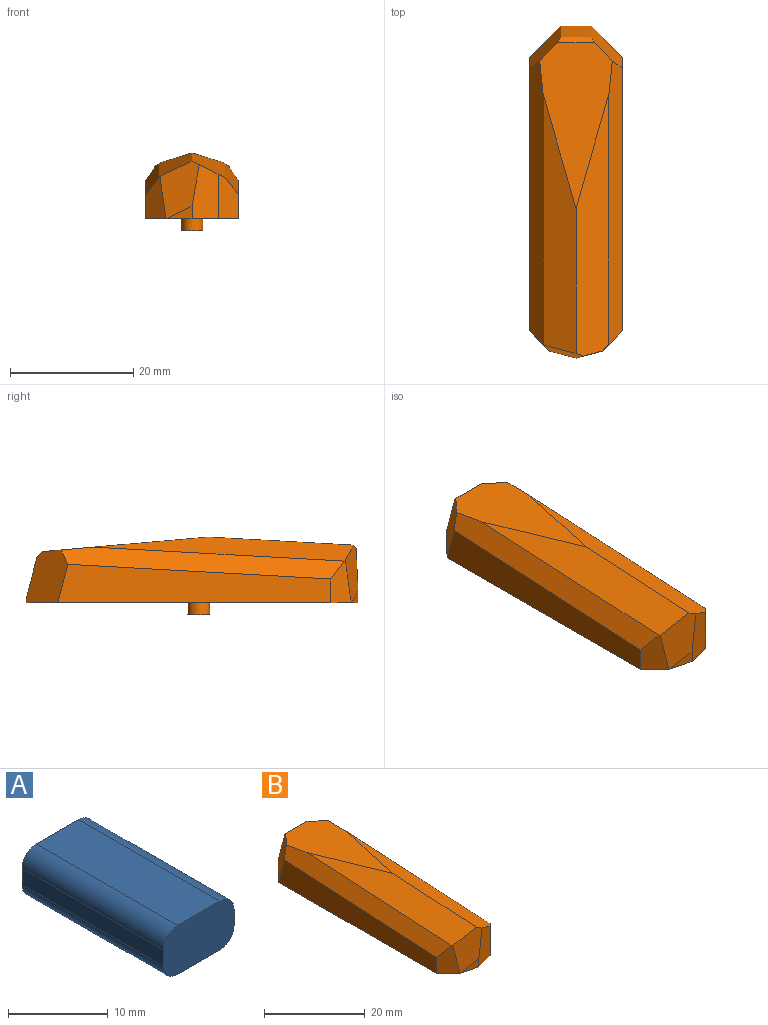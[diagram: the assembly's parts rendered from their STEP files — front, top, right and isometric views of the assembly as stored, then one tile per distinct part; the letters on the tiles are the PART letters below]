
ASSEMBLY  parts=2 mates=1
PART A: 10 faces, bbox 10x20x6 mm
  f0: plane 20x6mm, normal (0,0,-1), area 120mm2, adj f1,f2,f4,f8
  f1: cylinder r=2mm len=20mm, axis (0,1,0), area 62.8mm2, adj f0,f2,f4,f9
  f2: plane 10x6mm, normal (0,1,0), area 56.6mm2, adj f0,f1,f3,f5,f6,f7,f8,f9
  f3: cylinder r=2mm len=20mm, axis (0,-1,0), area 62.8mm2, adj f2,f4,f5,f9
  f4: plane 10x6mm, normal (0,-1,0), area 56.6mm2, adj f0,f1,f3,f5,f6,f7,f8,f9
  f5: plane 20x6mm, normal (0,0,1), area 120mm2, adj f2,f3,f4,f6
  f6: cylinder r=2mm len=20mm, axis (0,1,0), area 62.8mm2, adj f2,f4,f5,f7
  f7: plane 20x2mm, normal (1,0,0), area 40mm2, adj f2,f4,f6,f8
  f8: cylinder r=2mm len=20mm, axis (0,-1,0), area 62.8mm2, adj f0,f2,f4,f7
  f9: plane 20x2mm, normal (-1,0,0), area 40mm2, adj f1,f2,f3,f4
PART B: 51 faces, bbox 15x53.8x12.6 mm
  f0: plane 44.26x6.22mm, normal (1,0,0), area 219.2mm2, adj f1,f9,f10,f49
  f1: plane 45.86x5.16mm, normal (0.81,-0.03,0.58), area 162.1mm2, adj f0,f2,f8,f9,f49
  f2: plane 26.95x11.76mm, normal (0,0.09,1), area 186.4mm2, adj f1,f3,f5,f6,f7,f8,f49
  f3: plane 5.95x0.85mm, normal (0,0.71,0.71), area 6.4mm2, adj f2,f4,f5,f49
  f4: plane 6.88x4.74mm, normal (0,0.97,0.25), area 33.7mm2, adj f3,f5,f49,f50
  f5: plane 8.53x6.79mm, normal (-0.71,0.68,0.18), area 60mm2, adj f2,f3,f4,f6,f10,f44,f50
  f6: plane 45.86x5.16mm, normal (-0.81,-0.03,0.58), area 162.1mm2, adj f2,f5,f7,f44,f45
  f7: plane 42.1x5.34mm, normal (-0.45,-0.05,0.89), area 191.9mm2, adj f2,f6,f8,f45,f46
  f8: plane 42.53x5.34mm, normal (0.45,-0.05,0.89), area 195.2mm2, adj f1,f2,f7,f9,f46,f47
  f9: plane 7.22x3.28mm, normal (0.71,-0.71,0), area 27.2mm2, adj f0,f1,f8,f10,f47
  f10: plane 53.81x15mm, normal (0,0,-1), area 208.9mm2, adj f0,f5,f9,f11,f13,f15,f16,f32
  f11: plane 3.57x2.3mm, normal (0,-1,0), area 8.2mm2, adj f10,f12,f13,f36
  f12: plane 4.5x3.85mm, normal (0,-0.97,-0.25), area 17.8mm2, adj f11,f13,f14,f35,f36,f37
  f13: plane 4.15x4.01mm, normal (0.72,-0.7,0), area 16.4mm2, adj f10,f11,f12,f14,f15
  f14: plane 4.97x4.55mm, normal (0.71,-0.68,-0.18), area 24.6mm2, adj f12,f13,f15,f17,f24,f37
  f15: plane 42.87x6.53mm, normal (1,0,0), area 228.9mm2, adj f10,f13,f14,f16,f17
  f16: plane 6.31x2.24mm, normal (0.71,0.71,0), area 17.4mm2, adj f10,f15,f17,f30,f32
  f17: plane 43.56x3.75mm, normal (0.81,0.03,-0.58), area 87.8mm2, adj f14,f15,f16,f18,f19,f20,f24,f30
  f18: plane 9.43x1.2mm, normal (0,0,-1), area 11.3mm2, adj f17,f20,f38,f41
  f19: plane 10.17x1.2mm, normal (0,0,-1), area 12.1mm2, adj f17,f38,f39,f40
  f20: plane 9.34x1.64mm, normal (0,-1,0), area 10.7mm2, adj f17,f18,f22,f27,f30,f38
  f21: plane 1.29x0.68mm, normal (0,-0.09,-1), area 0.4mm2, adj f25,f26,f29
  f22: plane 3.38x3.24mm, normal (0,-0.09,-1), area 7.6mm2, adj f20,f27,f30,f42
  f23: plane 8.51x8mm, normal (0,-0.09,-1), area 49.9mm2, adj f28,f31,f40,f41
  f24: plane 10.39x9.42mm, normal (0,-0.09,-1), area 84.4mm2, adj f14,f17,f35,f37,f38,f39
  f25: cylinder r=0.65mm len=11.33mm, axis (0,0,-1), area 45.5mm2, adj f21,f26,f29,f43
  f26: plane 1.2x0.66mm, normal (-0.45,0.05,-0.89), area 0.5mm2, adj f21,f25,f29
  f27: plane 27.96x4.54mm, normal (-0.45,0.05,-0.89), area 132mm2, adj f20,f22,f30,f32,f33,f38,f42
  f28: plane 8x2.58mm, normal (-0.45,0.05,-0.89), area 12.8mm2, adj f23,f38,f40,f41
  f29: plane 1.2x0.66mm, normal (0.45,0.05,-0.89), area 0.5mm2, adj f21,f25,f26
  f30: plane 27.96x4.54mm, normal (0.45,0.05,-0.89), area 132mm2, adj f16,f17,f20,f22,f27,f32,f42
  f31: plane 8x2.58mm, normal (0.45,0.05,-0.89), area 12.8mm2, adj f17,f23,f40,f41
  f32: plane 8.09x7.12mm, normal (0,1,0), area 51.2mm2, adj f10,f16,f27,f30,f33
  f33: plane 6.31x2.24mm, normal (-0.71,0.71,0), area 17.4mm2, adj f10,f27,f32,f34,f38
  f34: plane 42.87x6.53mm, normal (-1,0,0), area 228.9mm2, adj f10,f33,f35,f36,f38
  f35: plane 4.97x4.55mm, normal (-0.71,-0.68,-0.18), area 24.6mm2, adj f12,f24,f34,f36,f37,f38
  f36: plane 4.15x4.01mm, normal (-0.72,-0.7,0), area 16.4mm2, adj f10,f11,f12,f34,f35
  f37: plane 4.29x0.31mm, normal (0,-0.71,-0.71), area 1.8mm2, adj f12,f14,f24,f35
  f38: plane 43.56x3.75mm, normal (-0.81,0.03,-0.58), area 87.8mm2, adj f18,f19,f20,f24,f27,f28,f33,f34
  f39: plane 10.17x0.73mm, normal (0,1,0), area 7.1mm2, adj f17,f19,f24,f38
  f40: plane 10.07x0.84mm, normal (0,-1,0), area 7.9mm2, adj f17,f19,f23,f28,f31,f38
  f41: plane 9.43x1.54mm, normal (0,1,0), area 10.7mm2, adj f17,f18,f23,f28,f31,f38
  f42: cylinder r=1.75mm len=11.27mm, axis (0,0,-1), area 118.7mm2, adj f22,f27,f30,f43
  f43: plane 3.5x3.5mm, normal (0,0,-1), area 8.3mm2, adj f25,f42
  f44: plane 44.26x6.22mm, normal (-1,0,0), area 219.2mm2, adj f5,f6,f10,f45
  f45: plane 6.79x3.28mm, normal (-0.71,-0.71,0), area 22.2mm2, adj f6,f7,f10,f44,f46
  f46: plane 9.31x6.37mm, normal (-0.29,-0.95,0.09), area 40.6mm2, adj f7,f8,f10,f45,f47,f48
  f47: plane 8.7x4.22mm, normal (0.25,-0.97,0), area 31.6mm2, adj f8,f9,f10,f46,f48
  f48: plane 4.14x2.01mm, normal (-0.25,-0.97,0), area 4.3mm2, adj f10,f46,f47
  f49: plane 8.53x6.79mm, normal (0.71,0.68,0.18), area 60mm2, adj f0,f1,f2,f3,f4,f10,f50
  f50: plane 5.01x0.54mm, normal (0,1,0), area 2.6mm2, adj f4,f5,f10,f49
PLACE A t=(22.4,0.64,-3.4)mm
PLACE B t=(22.4,12.45,-0.29)mm
MATE parallel A.f4 <-> B.f32  axis (0,-1,0) through (22.4,-9.36,-0.4)mm
